# Revit family: Kohler Stance 14760A-4ND-CP Family
name_source: partatom
category: Plumbing Fixtures
revit_build: Autodesk Revit 2018 (Build: 20170223_1515(x64)
units: mm (PartAtom-declared; Revit-internal decimal feet)

## family parameters
Cut with Voids When Loaded = No
Host = Face
OmniClass Number = 23.45.55.17
OmniClass Title = Mixing Faucets
Part Type = Normal
Room Calculation Point = No
Round Connector Dimension = Use Radius
Shared = No

## types (2) — shared parameters
CW Connection = Yes
Description = Stance™ single-control lavatory faucet
Disclaimer = Although care has been taken to ensure, to the best of our knowledge, that all data and information contained herein is accurate to the extent that it relates to either matters of fact or accepted practice at the time of issue. MDFC (Pty) Ltd assumes no responsibility for any errors in, or misinterpretation of, such data and/ or information or any loss or damage arising from, or related to its use
HW Connection = Yes
Height = 241 mm
Length = 235 mm
Manufacturer = Kohler Co
Model = Kohler Stance 14760A-4ND-CP
Telephone = 011 050 9000
Width = 67 mm
zero-valued in all types: CWFU, Default Elevation, HWFU, WFU

## per-type parameters (varying)
| type | Assembly Code | Finish | URL |
| Kohler Stance 14760A-4ND-CP |  | Chrome-Kohler-CP-Polished_Chrome |  |
| Nickel-Vibrant_Brushed_Nickel-BN | D2010400 | Nickel-Kohler-BN-Vibrant_Brushed_Nickel | http://www.us.kohler.com |

## geometry (parser evidence)
native form markers: Blend x4, Sweep x2
no freeform markers — native parametric forms only
